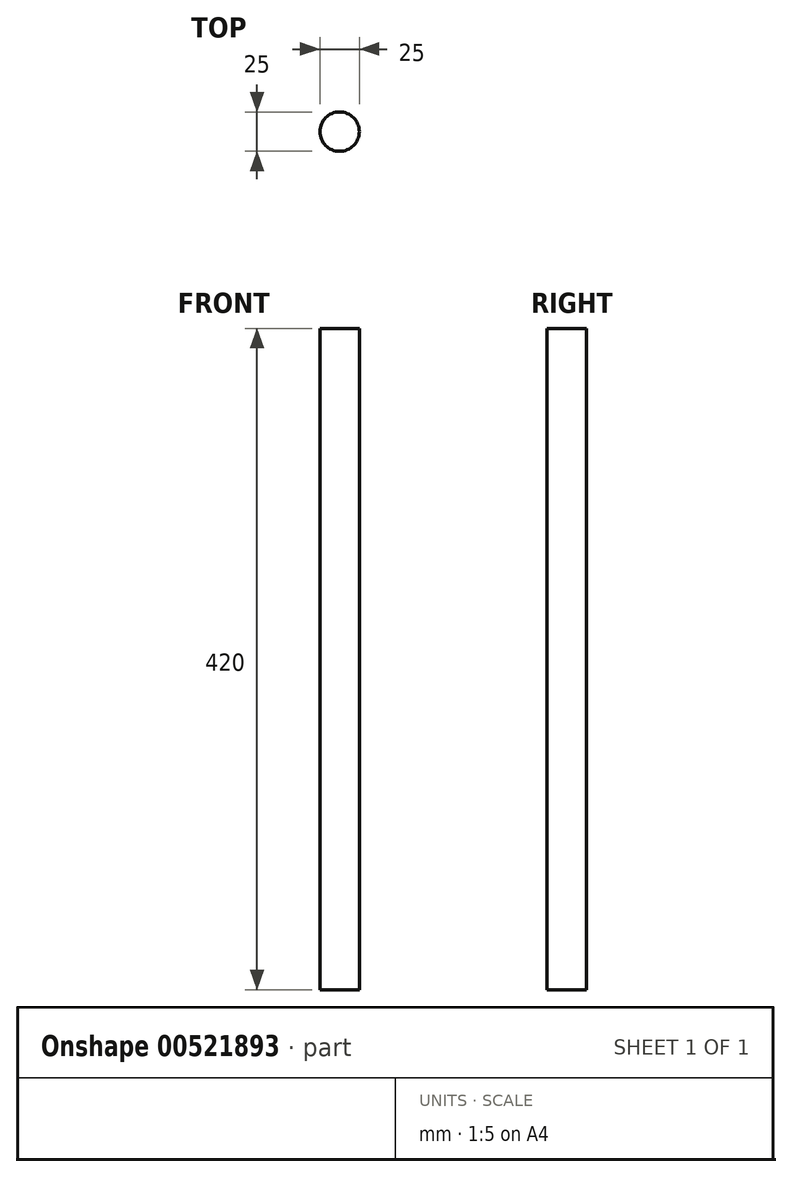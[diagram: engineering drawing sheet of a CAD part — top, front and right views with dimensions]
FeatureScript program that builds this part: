
annotation { "Feature Type Name" : "Feature", "Feature Type Description" : "" }
export const myFeature = defineFeature(function(context is Context, id is Id, definition is map)
    precondition{}
    {
        {
            var Q0;
            Q0=qCreatedBy(makeId("Top.planeOp"),FACE);
            var sketch = newSketch(context, id + "F0", { "sketchPlane" : qUnion([Q0])});
            skCircle(sketch, "E0", {"center": v(0, 0) * mm, "radius": 12.5 * mm});
            skSolve(sketch);
        }
        {
            var Q0;
            Q0 = qSketchRegion(id + "F0", true);
            extrude(context, id + "F1", {"entities" : qUnion([Q0]), "depth" : 420 * mm, "offsetDistance" : 25 * mm});
        }
    });
